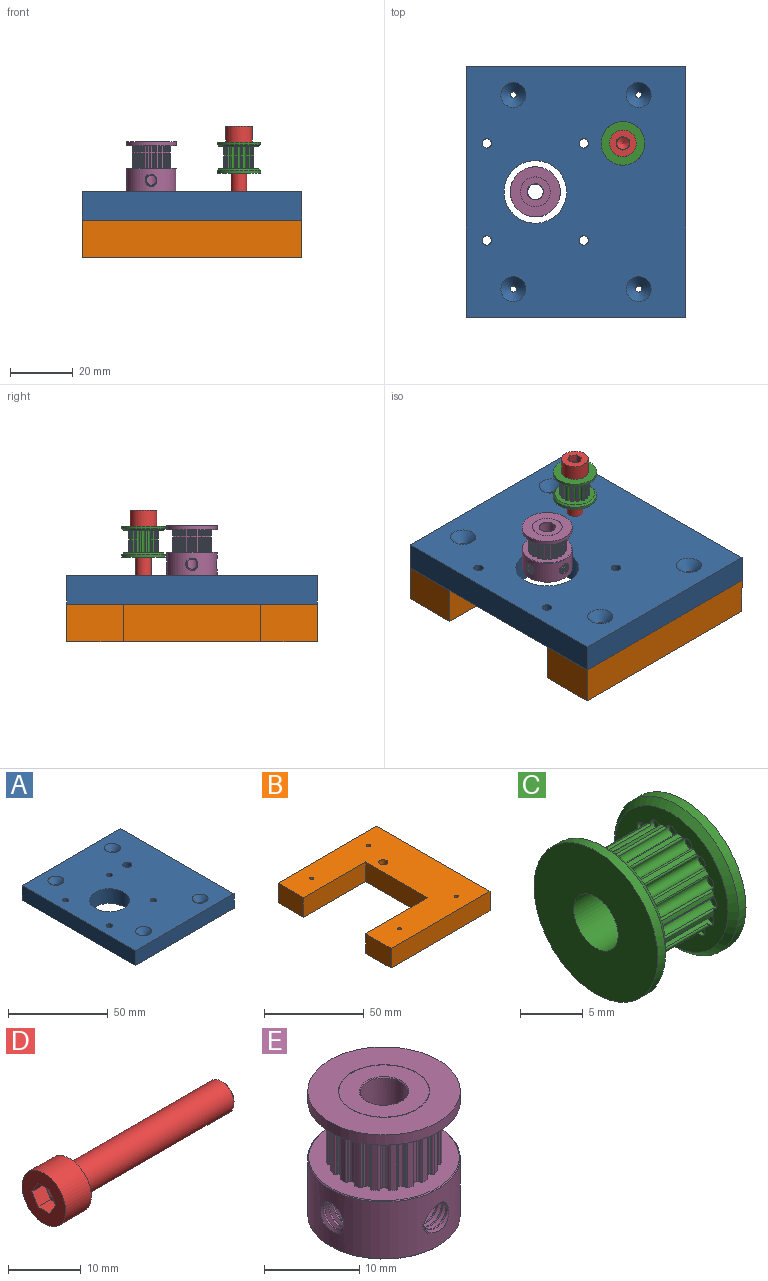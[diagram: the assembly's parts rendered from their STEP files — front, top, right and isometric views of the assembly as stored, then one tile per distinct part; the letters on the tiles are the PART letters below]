
ASSEMBLY  parts=5 mates=4
PART A: 20 faces, bbox 70x80x9 mm
  f0: plane 70x9mm, normal (0,1,0), area 630mm2, adj f1,f3,f5,f6
  f1: plane 80x9mm, normal (-1,0,0), area 720mm2, adj f0,f2,f5,f6
  f2: plane 70x9mm, normal (0,-1,0), area 630mm2, adj f1,f3,f5,f6
  f3: plane 80x9mm, normal (1,0,0), area 720mm2, adj f0,f2,f5,f6
  f4: cylinder r=10mm len=20mm, axis (0,0,-1), area 565.5mm2, adj f5,f6
  f5: plane 80x70mm, normal (0,0,1), area 5040.6mm2, adj f0,f1,f2,f3,f4,f11,f12,f13
  f6: plane 80x70mm, normal (0,0,-1), area 5229.1mm2, adj f0,f1,f2,f3,f4,f7,f8,f9
  f7: cylinder r=1mm len=6mm, axis (0,0,1), area 37.7mm2, adj f6,f18
  f8: cylinder r=1mm len=6mm, axis (0,0,1), area 37.7mm2, adj f6,f17
  f9: cylinder r=1mm len=6mm, axis (0,0,1), area 37.7mm2, adj f6,f19
  f10: cylinder r=1mm len=6mm, axis (0,0,1), area 37.7mm2, adj f6,f16
  f11: cylinder r=1.5mm len=9mm, axis (0,0,1), area 84.8mm2, adj f5,f6
  f12: cylinder r=1.5mm len=9mm, axis (0,0,1), area 84.8mm2, adj f5,f6
  f13: cylinder r=1.5mm len=9mm, axis (0,0,1), area 84.8mm2, adj f5,f6
  f14: cylinder r=1.5mm len=9mm, axis (0,0,1), area 84.8mm2, adj f5,f6
  f15: cylinder r=2.25mm len=9mm, axis (0,0,1), area 127.2mm2, adj f5,f6
  f16: cone r=1mm half-angle=45deg, axis (0,0,1), area 66.6mm2, adj f5,f10
  f17: cone r=1mm half-angle=45deg, axis (0,0,1), area 66.6mm2, adj f5,f8
  f18: cone r=1mm half-angle=45deg, axis (0,0,1), area 66.6mm2, adj f5,f7
  f19: cone r=1mm half-angle=45deg, axis (0,0,1), area 66.6mm2, adj f5,f9
PART B: 15 faces, bbox 70x80x12 mm
  f0: plane 70x12mm, normal (0,-1,0), area 840mm2, adj f1,f7,f8,f9
  f1: plane 80x12mm, normal (1,0,0), area 960mm2, adj f0,f2,f8,f9
  f2: plane 70x12mm, normal (0,1,0), area 840mm2, adj f1,f3,f8,f9
  f3: plane 18x12mm, normal (-1,0,0), area 216mm2, adj f2,f4,f8,f9
  f4: plane 44x12mm, normal (0,-1,0), area 528mm2, adj f3,f5,f8,f9
  f5: plane 44x12mm, normal (-1,0,0), area 528mm2, adj f4,f6,f8,f9
  f6: plane 44x12mm, normal (0,1,0), area 528mm2, adj f5,f7,f8,f9
  f7: plane 18x12mm, normal (-1,0,0), area 216mm2, adj f0,f6,f8,f9
  f8: plane 80x70mm, normal (0,0,1), area 3635.5mm2, adj f0,f1,f2,f3,f4,f5,f6,f7
  f9: plane 80x70mm, normal (0,0,-1), area 3635.5mm2, adj f0,f1,f2,f3,f4,f5,f6,f7
  f10: cylinder r=1mm len=12mm, axis (0,0,1), area 75.4mm2, adj f8,f9
  f11: cylinder r=1mm len=12mm, axis (0,0,1), area 75.4mm2, adj f8,f9
  f12: cylinder r=1mm len=12mm, axis (0,0,1), area 75.4mm2, adj f8,f9
  f13: cylinder r=1mm len=12mm, axis (0,0,1), area 75.4mm2, adj f8,f9
  f14: cylinder r=2.25mm len=12mm, axis (0,0,1), area 169.6mm2, adj f8,f9
PART C: 90 faces, bbox 9.9x13.9x13.9 mm
  f0: plane 13.9x13.9mm, normal (-1,0,0), area 132.1mm2, adj f32,f89
  f1: plane 13.9x13.9mm, normal (1,0,0), area 130.5mm2, adj f28,f29
  f2: cylinder r=0.16mm len=7mm, axis (-1,0,0), area 2mm2, adj f22,f33,f34,f50
  f3: cylinder r=0.16mm len=7mm, axis (-1,0,0), area 2mm2, adj f12,f33,f35,f50
  f4: cylinder r=0.16mm len=7mm, axis (-1,0,0), area 2mm2, adj f13,f33,f36,f50
  f5: cylinder r=0.16mm len=7mm, axis (-1,0,0), area 2mm2, adj f14,f33,f37,f50
  f6: cylinder r=0.16mm len=7mm, axis (1,0,0), area 2mm2, adj f15,f33,f37,f50
  f7: cylinder r=0.16mm len=7mm, axis (-1,0,0), area 2mm2, adj f15,f33,f38,f50
  f8: cylinder r=0.16mm len=7mm, axis (1,0,0), area 2mm2, adj f16,f33,f38,f50
  f9: cylinder r=0.16mm len=7mm, axis (1,0,0), area 2mm2, adj f17,f33,f39,f50
  f10: cylinder r=0.16mm len=7mm, axis (1,0,0), area 2mm2, adj f18,f33,f40,f50
  f11: cylinder r=0.16mm len=7mm, axis (1,0,0), area 2mm2, adj f19,f33,f41,f50
  f12: cylinder r=0.55mm len=7.35mm, axis (-1,0,0), area 13.6mm2, adj f3,f33,f50,f66,f87
  f13: cylinder r=0.55mm len=7.35mm, axis (-1,0,0), area 13.6mm2, adj f4,f33,f50,f65,f86
  f14: cylinder r=0.55mm len=7.35mm, axis (-1,0,0), area 13.6mm2, adj f5,f33,f50,f64,f85
  f15: cylinder r=0.55mm len=7.35mm, axis (-1,0,0), area 13.6mm2, adj f6,f7,f33,f50,f63
  f16: cylinder r=0.55mm len=7.35mm, axis (-1,0,0), area 13.6mm2, adj f8,f33,f50,f62,f84
  f17: cylinder r=0.55mm len=7.35mm, axis (-1,0,0), area 13.6mm2, adj f9,f33,f50,f61,f83
  f18: cylinder r=0.55mm len=7.35mm, axis (-1,0,0), area 13.6mm2, adj f10,f33,f50,f60,f82
  f19: cylinder r=0.55mm len=7.35mm, axis (-1,0,0), area 13.6mm2, adj f11,f33,f50,f59,f81
  f20: cylinder r=0.55mm len=7.35mm, axis (-1,0,0), area 13.6mm2, adj f33,f50,f58,f79,f80
  f21: cylinder r=0.55mm len=7.35mm, axis (-1,0,0), area 13.6mm2, adj f33,f50,f57,f77,f78
  f22: cylinder r=0.55mm len=7.35mm, axis (-1,0,0), area 13.6mm2, adj f2,f33,f50,f56,f88
  f23: cylinder r=0.55mm len=7.35mm, axis (-1,0,0), area 13.6mm2, adj f33,f50,f55,f75,f76
  f24: cylinder r=0.55mm len=7.35mm, axis (-1,0,0), area 13.6mm2, adj f33,f50,f54,f73,f74
  f25: cylinder r=0.55mm len=7.35mm, axis (-1,0,0), area 13.6mm2, adj f33,f50,f53,f71,f72
  f26: cylinder r=0.55mm len=7.35mm, axis (-1,0,0), area 13.6mm2, adj f33,f50,f52,f69,f70
  f27: cylinder r=0.55mm len=7.35mm, axis (-1,0,0), area 13.6mm2, adj f33,f50,f51,f67,f68
  f28: cone r=2.5mm half-angle=45deg, axis (1,0,0), area 2.3mm2, adj f1,f89
  f29: cylinder r=6.95mm len=13.9mm, axis (1,0,0), area 37.5mm2, adj f1,f31
  f30: cone r=6.95mm half-angle=43.7deg, axis (-1,0,0), area 34.3mm2, adj f32,f50
  f31: cone r=6.95mm half-angle=43.7deg, axis (1,0,0), area 34.3mm2, adj f29,f33
  f32: cylinder r=6.95mm len=13.9mm, axis (1,0,0), area 37.5mm2, adj f0,f30
  f33: plane 12.77x12.77mm, normal (-1,0,0), area 51.1mm2, adj f2,f3,f4,f5,f6,f7,f8,f9
  f34: cylinder r=4.84mm len=7mm, axis (1,0,0), area 3mm2, adj f2,f33,f50,f87
  f35: cylinder r=4.84mm len=7mm, axis (1,0,0), area 3mm2, adj f3,f33,f50,f86
  f36: cylinder r=4.84mm len=7mm, axis (1,0,0), area 3mm2, adj f4,f33,f50,f85
  f37: cylinder r=4.84mm len=7mm, axis (1,0,0), area 3mm2, adj f5,f6,f33,f50
  f38: cylinder r=4.84mm len=7mm, axis (1,0,0), area 3mm2, adj f7,f8,f33,f50
  f39: cylinder r=4.84mm len=7mm, axis (1,0,0), area 3mm2, adj f9,f33,f50,f84
  f40: cylinder r=4.84mm len=7mm, axis (1,0,0), area 3mm2, adj f10,f33,f50,f83
  f41: cylinder r=4.84mm len=7mm, axis (1,0,0), area 3mm2, adj f11,f33,f50,f82
  f42: cylinder r=4.84mm len=7mm, axis (1,0,0), area 3mm2, adj f33,f50,f80,f81
  f43: cylinder r=4.84mm len=7mm, axis (1,0,0), area 3mm2, adj f33,f50,f78,f79
  f44: cylinder r=4.84mm len=7mm, axis (1,0,0), area 3mm2, adj f33,f50,f76,f77
  f45: cylinder r=4.84mm len=7mm, axis (1,0,0), area 3mm2, adj f33,f50,f67,f88
  f46: cylinder r=4.84mm len=7mm, axis (1,0,0), area 3mm2, adj f33,f50,f74,f75
  f47: cylinder r=4.84mm len=7mm, axis (1,0,0), area 3mm2, adj f33,f50,f72,f73
  f48: cylinder r=4.84mm len=7mm, axis (1,0,0), area 3mm2, adj f33,f50,f70,f71
  f49: cylinder r=4.84mm len=7mm, axis (1,0,0), area 3mm2, adj f33,f50,f68,f69
  f50: plane 12.77x12.77mm, normal (1,0,0), area 66.3mm2, adj f2,f3,f4,f5,f6,f7,f8,f9
  f51: plane 1.1x1.1mm, normal (-1,0,0), area 1mm2, adj f27
  f52: plane 1.1x1.1mm, normal (-1,0,0), area 1mm2, adj f26
  f53: plane 1.1x1.1mm, normal (-1,0,0), area 1mm2, adj f25
  f54: plane 1.1x1.1mm, normal (-1,0,0), area 1mm2, adj f24
  f55: plane 1.1x1.1mm, normal (-1,0,0), area 1mm2, adj f23
  f56: plane 1.1x1.1mm, normal (-1,0,0), area 1mm2, adj f22
  f57: plane 1.1x1.1mm, normal (-1,0,0), area 1mm2, adj f21
  f58: plane 1.1x1.1mm, normal (-1,0,0), area 1mm2, adj f20
  f59: plane 1.1x1.1mm, normal (-1,0,0), area 1mm2, adj f19
  f60: plane 1.1x1.1mm, normal (-1,0,0), area 1mm2, adj f18
  f61: plane 1.1x1.1mm, normal (-1,0,0), area 1mm2, adj f17
  f62: plane 1.1x1.1mm, normal (-1,0,0), area 1mm2, adj f16
  f63: plane 1.1x1.1mm, normal (-1,0,0), area 1mm2, adj f15
  f64: plane 1.1x1.1mm, normal (-1,0,0), area 1mm2, adj f14
  f65: plane 1.1x1.1mm, normal (-1,0,0), area 1mm2, adj f13
  f66: plane 1.1x1.1mm, normal (-1,0,0), area 1mm2, adj f12
  f67: cylinder r=0.16mm len=7mm, axis (-1,0,0), area 2mm2, adj f27,f33,f45,f50
  f68: cylinder r=0.16mm len=7mm, axis (1,0,0), area 2mm2, adj f27,f33,f49,f50
  f69: cylinder r=0.16mm len=7mm, axis (-1,0,0), area 2mm2, adj f26,f33,f49,f50
  f70: cylinder r=0.16mm len=7mm, axis (1,0,0), area 2mm2, adj f26,f33,f48,f50
  f71: cylinder r=0.16mm len=7mm, axis (-1,0,0), area 2mm2, adj f25,f33,f48,f50
  f72: cylinder r=0.16mm len=7mm, axis (1,0,0), area 2mm2, adj f25,f33,f47,f50
  f73: cylinder r=0.16mm len=7mm, axis (-1,0,0), area 2mm2, adj f24,f33,f47,f50
  f74: cylinder r=0.16mm len=7mm, axis (1,0,0), area 2mm2, adj f24,f33,f46,f50
  f75: cylinder r=0.16mm len=7mm, axis (-1,0,0), area 2mm2, adj f23,f33,f46,f50
  f76: cylinder r=0.16mm len=7mm, axis (1,0,0), area 2mm2, adj f23,f33,f44,f50
  f77: cylinder r=0.16mm len=7mm, axis (-1,0,0), area 2mm2, adj f21,f33,f44,f50
  f78: cylinder r=0.16mm len=7mm, axis (1,0,0), area 2mm2, adj f21,f33,f43,f50
  f79: cylinder r=0.16mm len=7mm, axis (-1,0,0), area 2mm2, adj f20,f33,f43,f50
  f80: cylinder r=0.16mm len=7mm, axis (1,0,0), area 2mm2, adj f20,f33,f42,f50
  f81: cylinder r=0.16mm len=7mm, axis (-1,0,0), area 2mm2, adj f19,f33,f42,f50
  f82: cylinder r=0.16mm len=7mm, axis (-1,0,0), area 2mm2, adj f18,f33,f41,f50
  f83: cylinder r=0.16mm len=7mm, axis (-1,0,0), area 2mm2, adj f17,f33,f40,f50
  f84: cylinder r=0.16mm len=7mm, axis (-1,0,0), area 2mm2, adj f16,f33,f39,f50
  f85: cylinder r=0.16mm len=7mm, axis (1,0,0), area 2mm2, adj f14,f33,f36,f50
  f86: cylinder r=0.16mm len=7mm, axis (1,0,0), area 2mm2, adj f13,f33,f35,f50
  f87: cylinder r=0.16mm len=7mm, axis (1,0,0), area 2mm2, adj f12,f33,f34,f50
  f88: cylinder r=0.16mm len=7mm, axis (1,0,0), area 2mm2, adj f22,f33,f45,f50
  f89: cylinder r=2.5mm len=9.8mm, axis (1,0,0), area 153.9mm2, adj f0,f28
PART D: 14 faces, bbox 35x8.5x8.5 mm
  f0: cylinder r=4.25mm len=8.5mm, axis (-1,0,0), area 133.5mm2, adj f12,f13
  f1: cylinder r=2.5mm len=29.51mm, axis (-1,0,0), area 463.5mm2, adj f2,f12
  f2: cone r=2.25mm half-angle=45deg, axis (-1,0,0), area 9.8mm2, adj f1,f11
  f3: cone r=0.99mm half-angle=60deg, axis (-1,0,0), area 14.4mm2, adj f10
  f4: plane 2.5x2mm, normal (0,-0.87,-0.5), area 5.8mm2, adj f5,f9,f10,f13
  f5: plane 2.5x2mm, normal (0,-0.87,0.5), area 5.8mm2, adj f4,f6,f10,f13
  f6: plane 2.5x2.31mm, normal (0,0,1), area 5.8mm2, adj f5,f7,f10,f13
  f7: plane 2.5x2mm, normal (0,0.87,0.5), area 5.8mm2, adj f6,f8,f10,f13
  f8: plane 2.5x2mm, normal (0,0.87,-0.5), area 5.8mm2, adj f7,f9,f10,f13
  f9: plane 2.5x2.31mm, normal (0,0,-1), area 5.8mm2, adj f4,f8,f10,f13
  f10: plane 4.62x4mm, normal (-1,0,0), area 1.4mm2, adj f3,f4,f5,f6,f7,f8,f9
  f11: plane 4.02x4.02mm, normal (1,0,0), area 12.7mm2, adj f2
  f12: plane 8.5x8.5mm, normal (1,0,0), area 37.1mm2, adj f0,f1
  f13: plane 8.5x8.5mm, normal (-1,0,0), area 42.9mm2, adj f0,f4,f5,f6,f7,f8,f9
PART E: 204 faces, bbox 16.2x16.2x16 mm
  f0: plane 9.5x9.5mm, normal (0,0,-1), area 49.6mm2, adj f1,f203
  f1: cylinder r=4.75mm len=9.5mm, axis (0,0,-1), area 0.3mm2, adj f0,f2
  f2: plane 9.55x9.55mm, normal (0,0,-1), area 0.7mm2, adj f1,f3
  f3: cylinder r=4.77mm len=9.55mm, axis (0,0,-1), area 0.3mm2, adj f2,f4
  f4: plane 15.8x15.8mm, normal (0,0,-1), area 124.4mm2, adj f3,f5
  f5: cone r=7.9mm half-angle=45deg, axis (0,0,1), area 7.1mm2, adj f4,f6
  f6: cylinder r=8mm len=16mm, axis (0,0,1), area 347mm2, adj f5,f7,f194,f195,f196,f197,f198,f199
  f7: cylinder r=1.62mm len=5.74mm, axis (0,1,0), area -6.3mm2, adj f6,f8,f15,f194,f196
  f8: bspline ~3.71x1.94mm, area 1.5mm2, adj f7,f9,f15
  f9: cylinder r=2mm len=2.97mm, axis (0,1,0), area 0.3mm2, adj f8,f10,f15
  f10: bspline ~3.14x1.06mm, area 0.4mm2, adj f9,f11,f13,f14,f15
  f11: cylinder r=2mm len=0.01mm, axis (1,0,0), area 0mm2, adj f10,f12,f15
  f12: bspline ~1.73x0.78mm, area 0.3mm2, adj f11,f13,f14,f15
  f13: cylinder r=2mm len=1.31mm, axis (1,0,0), area 0mm2, adj f10,f12
  f14: cylinder r=2mm len=0.13mm, axis (1,0,0), area 0mm2, adj f10,f12,f15
  f15: cylinder r=2.5mm len=15.8mm, axis (0,0,-1), area 226.3mm2, adj f7,f8,f9,f10,f11,f12,f14,f16
  f16: bspline ~1.75x0.37mm, area 0mm2, adj f15,f19
  f17: cylinder r=1.62mm len=2.02mm, axis (0,1,0), area 0.3mm2, adj f15,f18,f196
  f18: bspline ~1.82x0.6mm, area 0.6mm2, adj f15,f17,f19
  f19: cylinder r=2mm len=1.82mm, axis (0,1,0), area 0.1mm2, adj f15,f16,f18
  f20: bspline ~2.85x1.22mm, area 0mm2, adj f15,f21
  f21: cylinder r=2mm len=2.71mm, axis (1,0,0), area 0.2mm2, adj f15,f20,f22
  f22: bspline ~3.37x1.71mm, area 1.3mm2, adj f15,f21,f200
  f23: cylinder r=1.62mm len=1.59mm, axis (-1,0,0), area 0mm2, adj f15,f24
  f24: bspline ~3.82x2.15mm, area 1.3mm2, adj f15,f23,f197
  f25: cone r=2.6mm half-angle=45deg, axis (0,0,1), area 2.3mm2, adj f15,f26
  f26: plane 9.5x9.5mm, normal (0,0,1), area 49.6mm2, adj f25,f27
  f27: cylinder r=4.75mm len=9.5mm, axis (0,0,1), area 0.3mm2, adj f26,f28
  f28: plane 9.55x9.55mm, normal (0,0,1), area 0.7mm2, adj f27,f29
  f29: cylinder r=4.77mm len=9.55mm, axis (0,0,1), area 0.3mm2, adj f28,f30
  f30: plane 16x16mm, normal (0,0,1), area 129.4mm2, adj f29,f31
  f31: cylinder r=8mm len=16mm, axis (0,0,-1), area 65.3mm2, adj f30,f32
  f32: plane 16x16mm, normal (0,0,-1), area 92.6mm2, adj f31,f33,f35,f36,f37,f38,f39,f40
  f33: cylinder r=6.1mm len=7.2mm, axis (0,0,-1), area 4.5mm2, adj f32,f34,f35,f193
  f34: plane 15.8x15.8mm, normal (0,0,1), area 87.6mm2, adj f33,f35,f36,f37,f38,f39,f40,f41
  f35: cylinder r=0.2mm len=7.2mm, axis (0,0,-1), area 2.2mm2, adj f32,f33,f34,f36
  f36: plane 7.2x0.11mm, normal (-0.81,0.59,0), area 1mm2, adj f32,f34,f35,f37
  f37: cylinder r=0.2mm len=7.2mm, axis (0,0,-1), area 2.1mm2, adj f32,f34,f36,f38
  f38: cylinder r=5.6mm len=7.2mm, axis (0,0,-1), area 2.9mm2, adj f32,f34,f37,f39
  f39: cylinder r=0.2mm len=7.2mm, axis (0,0,-1), area 2.1mm2, adj f32,f34,f38,f40
  f40: plane 7.2x0.11mm, normal (0.59,-0.81,0), area 1mm2, adj f32,f34,f39,f41
  f41: cylinder r=0.2mm len=7.2mm, axis (0,0,-1), area 2.2mm2, adj f32,f34,f40,f42
  f42: cylinder r=6.1mm len=7.2mm, axis (0,0,-1), area 4.5mm2, adj f32,f34,f41,f43
  f43: cylinder r=0.2mm len=7.2mm, axis (0,0,-1), area 2.2mm2, adj f32,f34,f42,f44
  f44: plane 7.2x0.11mm, normal (-0.59,0.81,0), area 1mm2, adj f32,f34,f43,f45
  f45: cylinder r=0.2mm len=7.2mm, axis (0,0,-1), area 2.1mm2, adj f32,f34,f44,f46
  f46: cylinder r=5.6mm len=7.2mm, axis (0,0,-1), area 2.9mm2, adj f32,f34,f45,f47
  f47: cylinder r=0.2mm len=7.2mm, axis (0,0,-1), area 2.1mm2, adj f32,f34,f46,f48
  f48: plane 7.2x0.13mm, normal (0.31,-0.95,0), area 1mm2, adj f32,f34,f47,f49
  f49: cylinder r=0.2mm len=7.2mm, axis (0,0,-1), area 2.2mm2, adj f32,f34,f48,f50
  f50: cylinder r=6.1mm len=7.2mm, axis (0,0,-1), area 4.5mm2, adj f32,f34,f49,f51
  f51: cylinder r=0.2mm len=7.2mm, axis (0,0,-1), area 2.2mm2, adj f32,f34,f50,f52
  f52: plane 7.2x0.13mm, normal (-0.31,0.95,0), area 1mm2, adj f32,f34,f51,f53
  f53: cylinder r=0.2mm len=7.2mm, axis (0,0,-1), area 2.1mm2, adj f32,f34,f52,f54
  f54: cylinder r=5.6mm len=7.2mm, axis (0,0,-1), area 2.9mm2, adj f32,f34,f53,f55
  f55: cylinder r=0.2mm len=7.2mm, axis (0,0,-1), area 2.1mm2, adj f32,f34,f54,f56
  f56: plane 7.2x0.13mm, normal (0,-1,0), area 1mm2, adj f32,f34,f55,f57
  f57: cylinder r=0.2mm len=7.2mm, axis (0,0,-1), area 2.2mm2, adj f32,f34,f56,f58
  f58: cylinder r=6.1mm len=7.2mm, axis (0,0,-1), area 4.5mm2, adj f32,f34,f57,f59
  f59: cylinder r=0.2mm len=7.2mm, axis (0,0,-1), area 2.2mm2, adj f32,f34,f58,f60
  f60: plane 7.2x0.13mm, normal (0,1,0), area 1mm2, adj f32,f34,f59,f61
  f61: cylinder r=0.2mm len=7.2mm, axis (0,0,-1), area 2.1mm2, adj f32,f34,f60,f62
  f62: cylinder r=5.6mm len=7.2mm, axis (0,0,-1), area 2.9mm2, adj f32,f34,f61,f63
  f63: cylinder r=0.2mm len=7.2mm, axis (0,0,-1), area 2.1mm2, adj f32,f34,f62,f64
  f64: plane 7.2x0.13mm, normal (-0.31,-0.95,0), area 1mm2, adj f32,f34,f63,f65
  f65: cylinder r=0.2mm len=7.2mm, axis (0,0,-1), area 2.2mm2, adj f32,f34,f64,f66
  f66: cylinder r=6.1mm len=7.2mm, axis (0,0,-1), area 4.5mm2, adj f32,f34,f65,f67
  f67: cylinder r=0.2mm len=7.2mm, axis (0,0,-1), area 2.2mm2, adj f32,f34,f66,f68
  f68: plane 7.2x0.13mm, normal (0.31,0.95,0), area 1mm2, adj f32,f34,f67,f69
  f69: cylinder r=0.2mm len=7.2mm, axis (0,0,-1), area 2.1mm2, adj f32,f34,f68,f70
  f70: cylinder r=5.6mm len=7.2mm, axis (0,0,-1), area 2.9mm2, adj f32,f34,f69,f71
  f71: cylinder r=0.2mm len=7.2mm, axis (0,0,-1), area 2.1mm2, adj f32,f34,f70,f72
  f72: plane 7.2x0.11mm, normal (-0.59,-0.81,0), area 1mm2, adj f32,f34,f71,f73
  f73: cylinder r=0.2mm len=7.2mm, axis (0,0,-1), area 2.2mm2, adj f32,f34,f72,f74
  f74: cylinder r=6.1mm len=7.2mm, axis (0,0,-1), area 4.5mm2, adj f32,f34,f73,f75
  f75: cylinder r=0.2mm len=7.2mm, axis (0,0,-1), area 2.2mm2, adj f32,f34,f74,f76
  f76: plane 7.2x0.11mm, normal (0.59,0.81,0), area 1mm2, adj f32,f34,f75,f77
  f77: cylinder r=0.2mm len=7.2mm, axis (0,0,-1), area 2.1mm2, adj f32,f34,f76,f78
  f78: cylinder r=5.6mm len=7.2mm, axis (0,0,-1), area 2.9mm2, adj f32,f34,f77,f79
  f79: cylinder r=0.2mm len=7.2mm, axis (0,0,-1), area 2.1mm2, adj f32,f34,f78,f80
  f80: plane 7.2x0.11mm, normal (-0.81,-0.59,0), area 1mm2, adj f32,f34,f79,f81
  f81: cylinder r=0.2mm len=7.2mm, axis (0,0,-1), area 2.2mm2, adj f32,f34,f80,f82
  f82: cylinder r=6.1mm len=7.2mm, axis (0,0,-1), area 4.5mm2, adj f32,f34,f81,f83
  f83: cylinder r=0.2mm len=7.2mm, axis (0,0,-1), area 2.2mm2, adj f32,f34,f82,f84
  f84: plane 7.2x0.11mm, normal (0.81,0.59,0), area 1mm2, adj f32,f34,f83,f85
  f85: cylinder r=0.2mm len=7.2mm, axis (0,0,-1), area 2.1mm2, adj f32,f34,f84,f86
  f86: cylinder r=5.6mm len=7.2mm, axis (0,0,-1), area 2.9mm2, adj f32,f34,f85,f87
  f87: cylinder r=0.2mm len=7.2mm, axis (0,0,-1), area 2.1mm2, adj f32,f34,f86,f88
  f88: plane 7.2x0.13mm, normal (-0.95,-0.31,0), area 1mm2, adj f32,f34,f87,f89
  f89: cylinder r=0.2mm len=7.2mm, axis (0,0,-1), area 2.2mm2, adj f32,f34,f88,f90
  f90: cylinder r=6.1mm len=7.2mm, axis (0,0,-1), area 4.5mm2, adj f32,f34,f89,f91
  f91: cylinder r=0.2mm len=7.2mm, axis (0,0,-1), area 2.2mm2, adj f32,f34,f90,f92
  f92: plane 7.2x0.13mm, normal (0.95,0.31,0), area 1mm2, adj f32,f34,f91,f93
  f93: cylinder r=0.2mm len=7.2mm, axis (0,0,-1), area 2.1mm2, adj f32,f34,f92,f94
  f94: cylinder r=5.6mm len=7.2mm, axis (0,0,-1), area 2.9mm2, adj f32,f34,f93,f95
  f95: cylinder r=0.2mm len=7.2mm, axis (0,0,-1), area 2.1mm2, adj f32,f34,f94,f96
  f96: plane 7.2x0.13mm, normal (-1,0,0), area 1mm2, adj f32,f34,f95,f97
  f97: cylinder r=0.2mm len=7.2mm, axis (0,0,-1), area 2.2mm2, adj f32,f34,f96,f98
  f98: cylinder r=6.1mm len=7.2mm, axis (0,0,-1), area 4.5mm2, adj f32,f34,f97,f99
  f99: cylinder r=0.2mm len=7.2mm, axis (0,0,-1), area 2.2mm2, adj f32,f34,f98,f100
  f100: plane 7.2x0.13mm, normal (1,0,0), area 1mm2, adj f32,f34,f99,f101
  f101: cylinder r=0.2mm len=7.2mm, axis (0,0,-1), area 2.1mm2, adj f32,f34,f100,f102
  f102: cylinder r=5.6mm len=7.2mm, axis (0,0,-1), area 2.9mm2, adj f32,f34,f101,f103
  f103: cylinder r=0.2mm len=7.2mm, axis (0,0,-1), area 2.1mm2, adj f32,f34,f102,f104
  f104: plane 7.2x0.13mm, normal (-0.95,0.31,0), area 1mm2, adj f32,f34,f103,f105
  f105: cylinder r=0.2mm len=7.2mm, axis (0,0,-1), area 2.2mm2, adj f32,f34,f104,f106
  f106: cylinder r=6.1mm len=7.2mm, axis (0,0,-1), area 4.5mm2, adj f32,f34,f105,f107
  f107: cylinder r=0.2mm len=7.2mm, axis (0,0,-1), area 2.2mm2, adj f32,f34,f106,f108
  f108: plane 7.2x0.13mm, normal (0.95,-0.31,0), area 1mm2, adj f32,f34,f107,f109
  f109: cylinder r=0.2mm len=7.2mm, axis (0,0,-1), area 2.1mm2, adj f32,f34,f108,f110
  f110: cylinder r=5.6mm len=7.2mm, axis (0,0,-1), area 2.9mm2, adj f32,f34,f109,f111
  f111: cylinder r=0.2mm len=7.2mm, axis (0,0,-1), area 2.1mm2, adj f32,f34,f110,f112
  f112: plane 7.2x0.11mm, normal (-0.81,0.59,0), area 1mm2, adj f32,f34,f111,f113
  f113: cylinder r=0.2mm len=7.2mm, axis (0,0,-1), area 2.2mm2, adj f32,f34,f112,f114
  f114: cylinder r=6.1mm len=7.2mm, axis (0,0,-1), area 4.5mm2, adj f32,f34,f113,f115
  f115: cylinder r=0.2mm len=7.2mm, axis (0,0,-1), area 2.2mm2, adj f32,f34,f114,f116
  f116: plane 7.2x0.11mm, normal (0.81,-0.59,0), area 1mm2, adj f32,f34,f115,f117
  f117: cylinder r=0.2mm len=7.2mm, axis (0,0,-1), area 2.1mm2, adj f32,f34,f116,f118
  f118: cylinder r=5.6mm len=7.2mm, axis (0,0,-1), area 2.9mm2, adj f32,f34,f117,f119
  f119: cylinder r=0.2mm len=7.2mm, axis (0,0,-1), area 2.1mm2, adj f32,f34,f118,f120
  f120: plane 7.2x0.11mm, normal (-0.59,0.81,0), area 1mm2, adj f32,f34,f119,f121
  f121: cylinder r=0.2mm len=7.2mm, axis (0,0,-1), area 2.2mm2, adj f32,f34,f120,f122
  f122: cylinder r=6.1mm len=7.2mm, axis (0,0,-1), area 4.5mm2, adj f32,f34,f121,f123
  f123: cylinder r=0.2mm len=7.2mm, axis (0,0,-1), area 2.2mm2, adj f32,f34,f122,f124
  f124: plane 7.2x0.11mm, normal (0.59,-0.81,0), area 1mm2, adj f32,f34,f123,f125
  f125: cylinder r=0.2mm len=7.2mm, axis (0,0,-1), area 2.1mm2, adj f32,f34,f124,f126
  f126: cylinder r=5.6mm len=7.2mm, axis (0,0,-1), area 2.9mm2, adj f32,f34,f125,f127
  f127: cylinder r=0.2mm len=7.2mm, axis (0,0,-1), area 2.1mm2, adj f32,f34,f126,f128
  f128: plane 7.2x0.13mm, normal (-0.31,0.95,0), area 1mm2, adj f32,f34,f127,f129
  f129: cylinder r=0.2mm len=7.2mm, axis (0,0,-1), area 2.2mm2, adj f32,f34,f128,f130
  f130: cylinder r=6.1mm len=7.2mm, axis (0,0,-1), area 4.5mm2, adj f32,f34,f129,f131
  f131: cylinder r=0.2mm len=7.2mm, axis (0,0,-1), area 2.2mm2, adj f32,f34,f130,f132
  f132: plane 7.2x0.13mm, normal (0.31,-0.95,0), area 1mm2, adj f32,f34,f131,f133
  f133: cylinder r=0.2mm len=7.2mm, axis (0,0,-1), area 2.1mm2, adj f32,f34,f132,f134
  f134: cylinder r=5.6mm len=7.2mm, axis (0,0,-1), area 2.9mm2, adj f32,f34,f133,f135
  f135: cylinder r=0.2mm len=7.2mm, axis (0,0,-1), area 2.1mm2, adj f32,f34,f134,f136
  f136: plane 7.2x0.13mm, normal (0,1,0), area 1mm2, adj f32,f34,f135,f137
  f137: cylinder r=0.2mm len=7.2mm, axis (0,0,-1), area 2.2mm2, adj f32,f34,f136,f138
  f138: cylinder r=6.1mm len=7.2mm, axis (0,0,-1), area 4.5mm2, adj f32,f34,f137,f139
  f139: cylinder r=0.2mm len=7.2mm, axis (0,0,-1), area 2.2mm2, adj f32,f34,f138,f140
  f140: plane 7.2x0.13mm, normal (0,-1,0), area 1mm2, adj f32,f34,f139,f141
  f141: cylinder r=0.2mm len=7.2mm, axis (0,0,-1), area 2.1mm2, adj f32,f34,f140,f142
  f142: cylinder r=5.6mm len=7.2mm, axis (0,0,-1), area 2.9mm2, adj f32,f34,f141,f143
  f143: cylinder r=0.2mm len=7.2mm, axis (0,0,-1), area 2.1mm2, adj f32,f34,f142,f144
  f144: plane 7.2x0.13mm, normal (0.31,0.95,0), area 1mm2, adj f32,f34,f143,f145
  f145: cylinder r=0.2mm len=7.2mm, axis (0,0,-1), area 2.2mm2, adj f32,f34,f144,f146
  f146: cylinder r=6.1mm len=7.2mm, axis (0,0,-1), area 4.5mm2, adj f32,f34,f145,f147
  f147: cylinder r=0.2mm len=7.2mm, axis (0,0,-1), area 2.2mm2, adj f32,f34,f146,f148
  f148: plane 7.2x0.13mm, normal (-0.31,-0.95,0), area 1mm2, adj f32,f34,f147,f149
  f149: cylinder r=0.2mm len=7.2mm, axis (0,0,-1), area 2.1mm2, adj f32,f34,f148,f150
  f150: cylinder r=5.6mm len=7.2mm, axis (0,0,-1), area 2.9mm2, adj f32,f34,f149,f151
  f151: cylinder r=0.2mm len=7.2mm, axis (0,0,-1), area 2.1mm2, adj f32,f34,f150,f152
  f152: plane 7.2x0.11mm, normal (0.59,0.81,0), area 1mm2, adj f32,f34,f151,f153
  f153: cylinder r=0.2mm len=7.2mm, axis (0,0,-1), area 2.2mm2, adj f32,f34,f152,f154
  f154: cylinder r=6.1mm len=7.2mm, axis (0,0,-1), area 4.5mm2, adj f32,f34,f153,f155
  f155: cylinder r=0.2mm len=7.2mm, axis (0,0,-1), area 2.2mm2, adj f32,f34,f154,f156
  f156: plane 7.2x0.11mm, normal (-0.59,-0.81,0), area 1mm2, adj f32,f34,f155,f157
  f157: cylinder r=0.2mm len=7.2mm, axis (0,0,-1), area 2.1mm2, adj f32,f34,f156,f158
  f158: cylinder r=5.6mm len=7.2mm, axis (0,0,-1), area 2.9mm2, adj f32,f34,f157,f159
  f159: cylinder r=0.2mm len=7.2mm, axis (0,0,-1), area 2.1mm2, adj f32,f34,f158,f160
  f160: plane 7.2x0.11mm, normal (0.81,0.59,0), area 1mm2, adj f32,f34,f159,f161
  f161: cylinder r=0.2mm len=7.2mm, axis (0,0,-1), area 2.2mm2, adj f32,f34,f160,f162
  f162: cylinder r=6.1mm len=7.2mm, axis (0,0,-1), area 4.5mm2, adj f32,f34,f161,f163
  f163: cylinder r=0.2mm len=7.2mm, axis (0,0,-1), area 2.2mm2, adj f32,f34,f162,f164
  f164: plane 7.2x0.11mm, normal (-0.81,-0.59,0), area 1mm2, adj f32,f34,f163,f165
  f165: cylinder r=0.2mm len=7.2mm, axis (0,0,-1), area 2.1mm2, adj f32,f34,f164,f166
  f166: cylinder r=5.6mm len=7.2mm, axis (0,0,-1), area 2.9mm2, adj f32,f34,f165,f167
  f167: cylinder r=0.2mm len=7.2mm, axis (0,0,-1), area 2.1mm2, adj f32,f34,f166,f168
  f168: plane 7.2x0.13mm, normal (0.95,0.31,0), area 1mm2, adj f32,f34,f167,f169
  f169: cylinder r=0.2mm len=7.2mm, axis (0,0,-1), area 2.2mm2, adj f32,f34,f168,f170
  f170: cylinder r=6.1mm len=7.2mm, axis (0,0,-1), area 4.5mm2, adj f32,f34,f169,f171
  f171: cylinder r=0.2mm len=7.2mm, axis (0,0,-1), area 2.2mm2, adj f32,f34,f170,f172
  f172: plane 7.2x0.13mm, normal (-0.95,-0.31,0), area 1mm2, adj f32,f34,f171,f173
  f173: cylinder r=0.2mm len=7.2mm, axis (0,0,-1), area 2.1mm2, adj f32,f34,f172,f174
  f174: cylinder r=5.6mm len=7.2mm, axis (0,0,-1), area 2.9mm2, adj f32,f34,f173,f175
  f175: cylinder r=0.2mm len=7.2mm, axis (0,0,-1), area 2.1mm2, adj f32,f34,f174,f176
  f176: plane 7.2x0.13mm, normal (1,0,0), area 1mm2, adj f32,f34,f175,f177
  f177: cylinder r=0.2mm len=7.2mm, axis (0,0,-1), area 2.2mm2, adj f32,f34,f176,f178
  f178: cylinder r=6.1mm len=7.2mm, axis (0,0,-1), area 4.5mm2, adj f32,f34,f177,f179
  f179: cylinder r=0.2mm len=7.2mm, axis (0,0,-1), area 2.2mm2, adj f32,f34,f178,f180
  f180: plane 7.2x0.13mm, normal (-1,0,0), area 1mm2, adj f32,f34,f179,f181
  f181: cylinder r=0.2mm len=7.2mm, axis (0,0,-1), area 2.1mm2, adj f32,f34,f180,f182
  f182: cylinder r=5.6mm len=7.2mm, axis (0,0,-1), area 2.9mm2, adj f32,f34,f181,f183
  f183: cylinder r=0.2mm len=7.2mm, axis (0,0,-1), area 2.1mm2, adj f32,f34,f182,f184
  f184: plane 7.2x0.13mm, normal (0.95,-0.31,0), area 1mm2, adj f32,f34,f183,f185
  f185: cylinder r=0.2mm len=7.2mm, axis (0,0,-1), area 2.2mm2, adj f32,f34,f184,f186
  f186: cylinder r=6.1mm len=7.2mm, axis (0,0,-1), area 4.5mm2, adj f32,f34,f185,f187
  f187: cylinder r=0.2mm len=7.2mm, axis (0,0,-1), area 2.2mm2, adj f32,f34,f186,f188
  f188: plane 7.2x0.13mm, normal (-0.95,0.31,0), area 1mm2, adj f32,f34,f187,f189
  f189: cylinder r=0.2mm len=7.2mm, axis (0,0,-1), area 2.1mm2, adj f32,f34,f188,f190
  f190: cylinder r=5.6mm len=7.2mm, axis (0,0,-1), area 2.9mm2, adj f32,f34,f189,f191
  f191: cylinder r=0.2mm len=7.2mm, axis (0,0,-1), area 2.1mm2, adj f32,f34,f190,f192
  f192: plane 7.2x0.11mm, normal (0.81,-0.59,0), area 1mm2, adj f32,f34,f191,f193
  f193: cylinder r=0.2mm len=7.2mm, axis (0,0,-1), area 2.2mm2, adj f32,f33,f34,f192
  f194: bspline ~5.87x4mm, area 38.9mm2, adj f6,f7,f15,f195
  f195: cylinder r=2mm len=5.68mm, axis (0,1,0), area 6.8mm2, adj f6,f15,f194,f196
  f196: bspline ~6.16x4mm, area 41.1mm2, adj f6,f7,f15,f17,f195
  f197: cylinder r=2mm len=5.7mm, axis (1,0,0), area 7.9mm2, adj f6,f15,f24,f199,f202
  f198: cone r=8mm half-angle=45deg, axis (0,0,-1), area 7.1mm2, adj f6,f34
  f199: bspline ~5.94x4.62mm, area 39.6mm2, adj f6,f15,f197,f200
  f200: cylinder r=1.62mm len=5.76mm, axis (-1,0,0), area 15.3mm2, adj f6,f15,f22,f199,f202
  f201: cylinder r=1.62mm len=1.03mm, axis (-1,0,0), area 0mm2, adj f6,f202
  f202: bspline ~5.87x4mm, area 40mm2, adj f6,f15,f197,f200,f201
  f203: cone r=2.5mm half-angle=45deg, axis (0,0,-1), area 2.3mm2, adj f0,f15
PLACE A t=(-249.31,-77.84,-133.73)mm
PLACE B t=(-249.31,-77.84,-133.73)mm
PLACE C rot(axis=(0,-1,0),90deg) t=(-444.31,45.16,482.37)mm
PLACE D rot(axis=(0,1,0),90deg) t=(-444.31,45.16,497.67)mm
PLACE E rot(axis=(-0.01,0,1),0deg) t=(-472.31,29.66,489.27)mm
MATE fastened A.f9 <-> B.f12  axis (0,0,-1) through (-479.31,-1.34,472.77)mm
MATE fastened D.f0 <-> C.f47  axis (0,0,-1) through (-444.31,45.16,497.67)mm
MATE revolute A.f15 <-> C.f89  axis (0,0,1) through (-444.31,45.16,481.77)mm
MATE revolute E.f1 <-> A.f4  axis (0,0,-1) through (-472.31,29.66,481.77)mm
